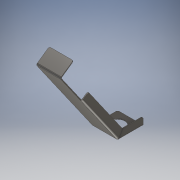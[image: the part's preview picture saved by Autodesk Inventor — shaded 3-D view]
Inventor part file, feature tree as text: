
AUTODESK INVENTOR PART (.ipt)
format: ipt  version: 2018 (Build 220112000, 112)  size: 189,440 bytes
history: native  units: mm
features: other x19, sketch x6, hole x1
ambient origin geometry x8: Origin, YZ Plane, XZ Plane, XY Plane, X Axis, Y Axis, Z Axis, Center Point
bodies: Solido1 (feature_tree)
feature tree (26):
  other  "Faccia1"
  hole  "Foro1"  [1 undecoded]
  other  "Flangia1"
  other  "Flangia2"
  other  "Flangia3"
  other  "Flangia4"
  other  "Arrotondamento angolo1"
  sketch  "Schizzo1"
  other  "Piano1"
  sketch  "Schizzo2"
  sketch  "Schizzo3"
  other  "Piano2"
  other  "Piega (Bend)1"
  other  "Angolo1"
  sketch  "Schizzo4"
  other  "Piano3"
  other  "Piega (Bend)2"
  other  "Angolo2"
  sketch  "Schizzo5"
  other  "Piano4"
  other  "Piega (Bend)3"
  other  "Angolo3"
  sketch  "Schizzo6"
  other  "Piano5"
  other  "Piega (Bend)4"
  other  "Angolo4"
note: 1 required parameter value undecoded (feature->parameter linkage not recoverable at this tier; creation-order binding heuristic only, values carry confidence <= 0.55)
